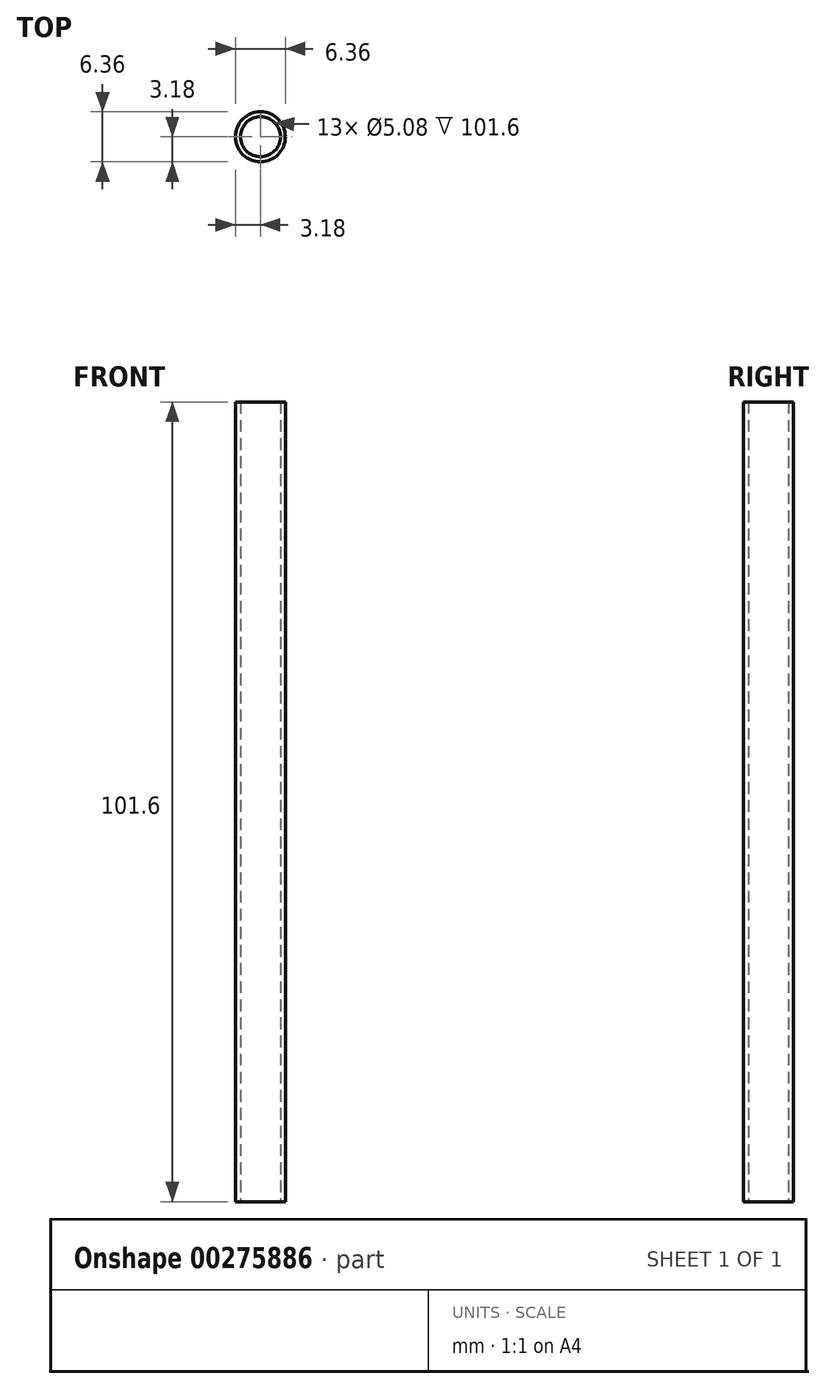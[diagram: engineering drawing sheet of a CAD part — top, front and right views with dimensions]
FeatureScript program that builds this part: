
annotation { "Feature Type Name" : "Feature", "Feature Type Description" : "" }
export const myFeature = defineFeature(function(context is Context, id is Id, definition is map)
    precondition{}
    {
        {
            var Q0;
            Q0=qCreatedBy(makeId("Top.planeOp"),FACE);
            var sketch = newSketch(context, id + "F0", { "sketchPlane" : qUnion([Q0])});
            skCircle(sketch, "E0", {"center": v(0, 0) * mm, "radius": 3.18 * mm});
            skCircle(sketch, "E1", {"center": v(0, 0) * mm, "radius": 2.54 * mm});
            skSolve(sketch);
        }
        {
            var Q0;
            Q0 = qSketchRegion(id + "F0", true);
            extrude(context, id + "F1", {"entities" : qUnion([Q0]), "depth" : 101.6 * mm});
        }
    });
